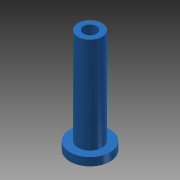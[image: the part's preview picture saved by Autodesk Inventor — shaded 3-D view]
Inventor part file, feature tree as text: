
AUTODESK INVENTOR PART (.ipt)
format: ipt  version: 2013 SP2 (Build 170200200, 200)  size: 81,920 bytes
history: native  units: mm
features: extrude x2, sketch x2
ambient origin geometry x8: Origin, YZ Plane, XZ Plane, XY Plane, X Axis, Y Axis, Z Axis, Center Point
bodies: Solid1 (feature_tree)
feature tree (4):
  extrude  "Extrusion1"  Depth=6.0mm
  extrude  "Extrusion2"  Depth=10.0mm
  sketch  "Sketch1"  dims[d0=3.3mm d1=6.0mm]
  sketch  "Sketch2"  dims[d2=26.0mm d3=0.0mm d4=10.0mm d5=2.0mm d6=0.0mm]
